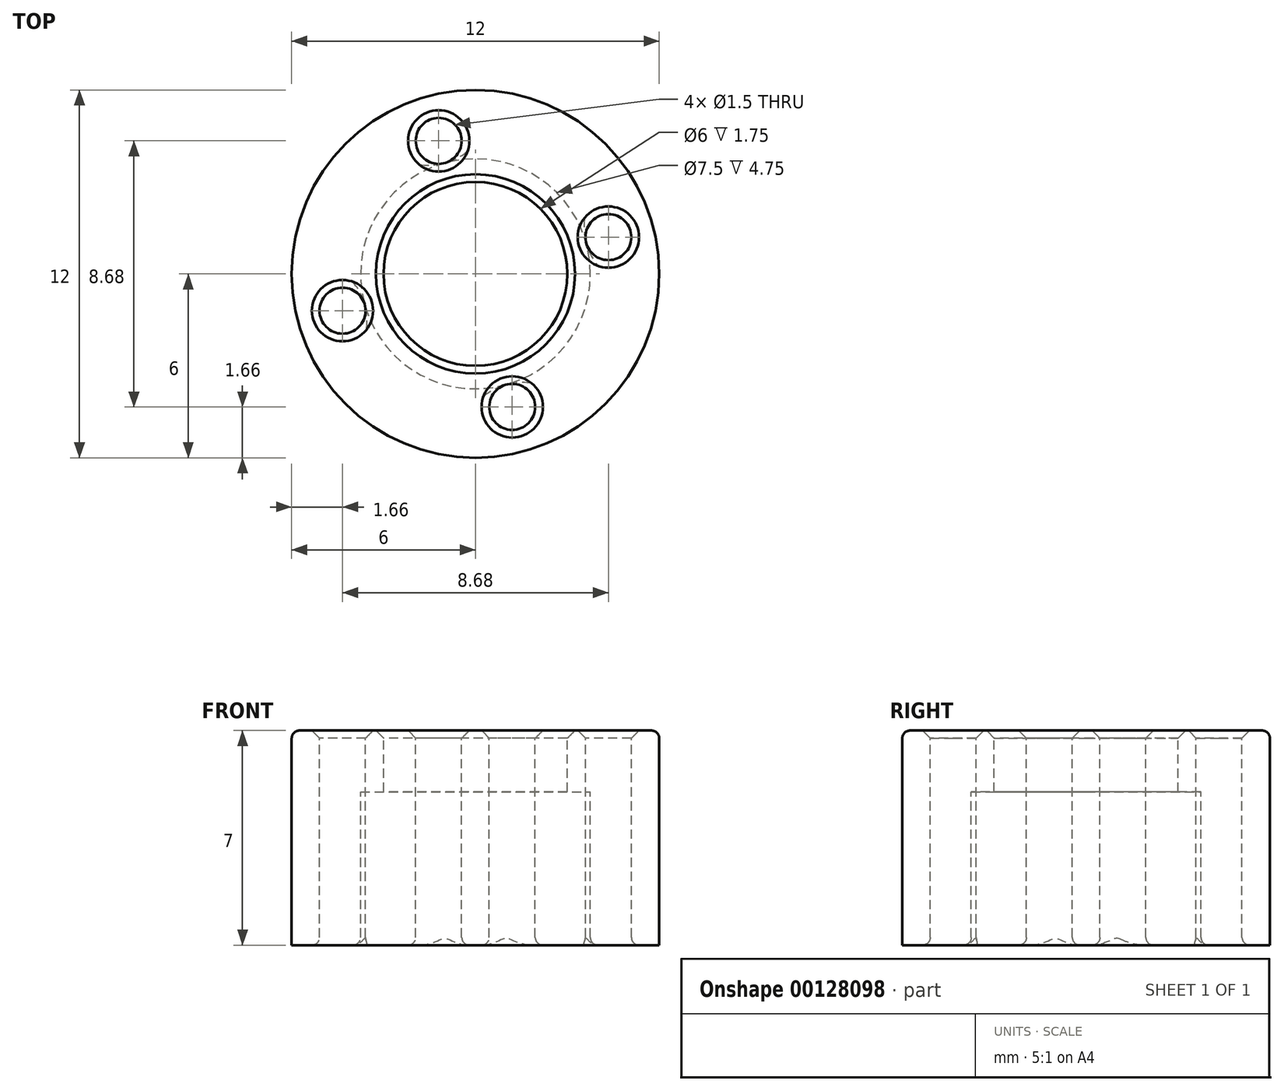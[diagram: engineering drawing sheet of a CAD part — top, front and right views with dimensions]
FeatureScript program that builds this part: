
annotation { "Feature Type Name" : "Feature", "Feature Type Description" : "" }
export const myFeature = defineFeature(function(context is Context, id is Id, definition is map)
    precondition{}
    {
        {
            var Q0;
            Q0=qCreatedBy(makeId("Top.planeOp"),FACE);
            var sketch = newSketch(context, id + "F0", { "sketchPlane" : qUnion([Q0])});
            skCircle(sketch, "E0", {"center": v(0, 0) * mm, "radius": 6 * mm});
            skCircle(sketch, "E1", {"center": v(0, 0) * mm, "radius": 3 * mm});
            skPoint(sketch, "E2", {"position": v(1.2, -4.34) * mm});
            skPoint(sketch, "E3.1.0", {"position": v(4.34, 1.2) * mm});
            skPoint(sketch, "E3.2.0", {"position": v(-1.2, 4.34) * mm});
            skPoint(sketch, "E3.3.0", {"position": v(-4.34, -1.2) * mm});
            skSolve(sketch);
        }
        {
            var Q0;
            Q0=makeQuery(id+"F0.imprint","IMPRINT",FACE,{"disambiguationData":[TD([[makeQuery(id+"F0.imprint","IMPRINT",EDGE,{"derivedFrom":sQuery(id+"F0.wireOp",EDGE,"E0")}),1.0]])]});
            extrude(context, id + "F1", {"entities" : qUnion([Q0]), "oppositeDirection" : true, "depth" : 2 * mm});
        }
        {
            var Q0;
            Q0=sQuery(id+"F0.wireOp",VERTEX,"E3.2.0");
            var Q1;
            Q1=sQuery(id+"F0.wireOp",VERTEX,"E2");
            var Q2;
            Q2=sQuery(id+"F0.wireOp",VERTEX,"E3.3.0");
            var Q3;
            Q3=sQuery(id+"F0.wireOp",VERTEX,"E3.1.0");
            var Q4;
            Q4=makeQuery(id+"F1.opExtrude","SWEPT_BODY",BODY,{"disambiguationData":[OSD([sQuery(id+"F0.wireOp",EDGE,"E0"),sQuery(id+"F0.wireOp",EDGE,"E1")])]});
            hole(context, id + "F2", {"style" : HoleStyle.C_SINK, "endStyle" : HoleEndStyle.THROUGH, "holeDiameter" : 1.5 * mm, "cSinkDiameter" : 2 * mm, "cSinkAngle" : 90 * degree, "locations" : qUnion([Q0, Q1, Q2, Q3]), "scope" : qUnion([Q4]), "isTappedThrough" : true});
        }
        {
            var Q0;
            Q0=makeQuery(id+"F1.opExtrude","CAP_EDGE",EDGE,{"disambiguationData":[OSD([sQuery(id+"F0.wireOp",EDGE,"E1")])],"isStart":true});
            chamfer(context, id + "F3", {"entities" : qUnion([Q0]), "width" : .25 * mm, "tangentPropagation" : true});
        }
        {
            var Q0;
            Q0=makeQuery(id+"F1.opExtrude","CAP_FACE",FACE,{"disambiguationData":[OSD([sQuery(id+"F0.wireOp",EDGE,"E0"),sQuery(id+"F0.wireOp",EDGE,"E1")])],"isStart":false});
            var sketch = newSketch(context, id + "F4", { "sketchPlane" : qUnion([Q0])});
            skCircle(sketch, "E4.0", {"center": v(0, 0) * mm, "radius": 3.75 * mm});
            skSolve(sketch);
        }
        {
            var Q0;
            Q0=makeQuery(id+"F4.imprint","IMPRINT",FACE,{"disambiguationData":[TD([[makeQuery(id+"F4.imprint","IMPRINT",EDGE,{"derivedFrom":sQuery(id+"F4.wireOp",EDGE,"E4.0")}),-1.0]])]});
            extrude(context, id + "F5", {"entities" : qUnion([Q0]), "operationType" : NewBodyOperationType.ADD, "depth" : 5 * mm});
        }
        {
            var Q0;
            Q0=makeQuery(id+"F5.opExtrude","CAP_EDGE",EDGE,{"disambiguationData":[OSD([sQuery(id+"F0.wireOp",EDGE,"E1")])],"isStart":false});
            var Q1;
            Q1=makeQuery(id+"F5.opExtrude","CAP_EDGE",EDGE,{"disambiguationData":[OSD([sQuery(id+"F4.wireOp",EDGE,"E4.0")])],"isStart":false});
            fillet(context, id + "F6", {"entities" : qUnion([Q0, Q1]), "radius" : .25 * mm, "allowEdgeOverflow" : false});
        }
        {
            var Q0;
            Q0=makeQuery(id+"F1.opExtrude","CAP_EDGE",EDGE,{"disambiguationData":[OSD([sQuery(id+"F0.wireOp",EDGE,"E0")])],"isStart":true});
            var Q1;
            Q1=makeQuery(id+"F1.opExtrude","CAP_EDGE",EDGE,{"disambiguationData":[OSD([sQuery(id+"F0.wireOp",EDGE,"E0")])],"isStart":false});
            fillet(context, id + "F7", {"entities" : qUnion([Q0, Q1]), "radius" : .25 * mm, "tangentPropagation" : true, "allowEdgeOverflow" : false});
        }
    });
